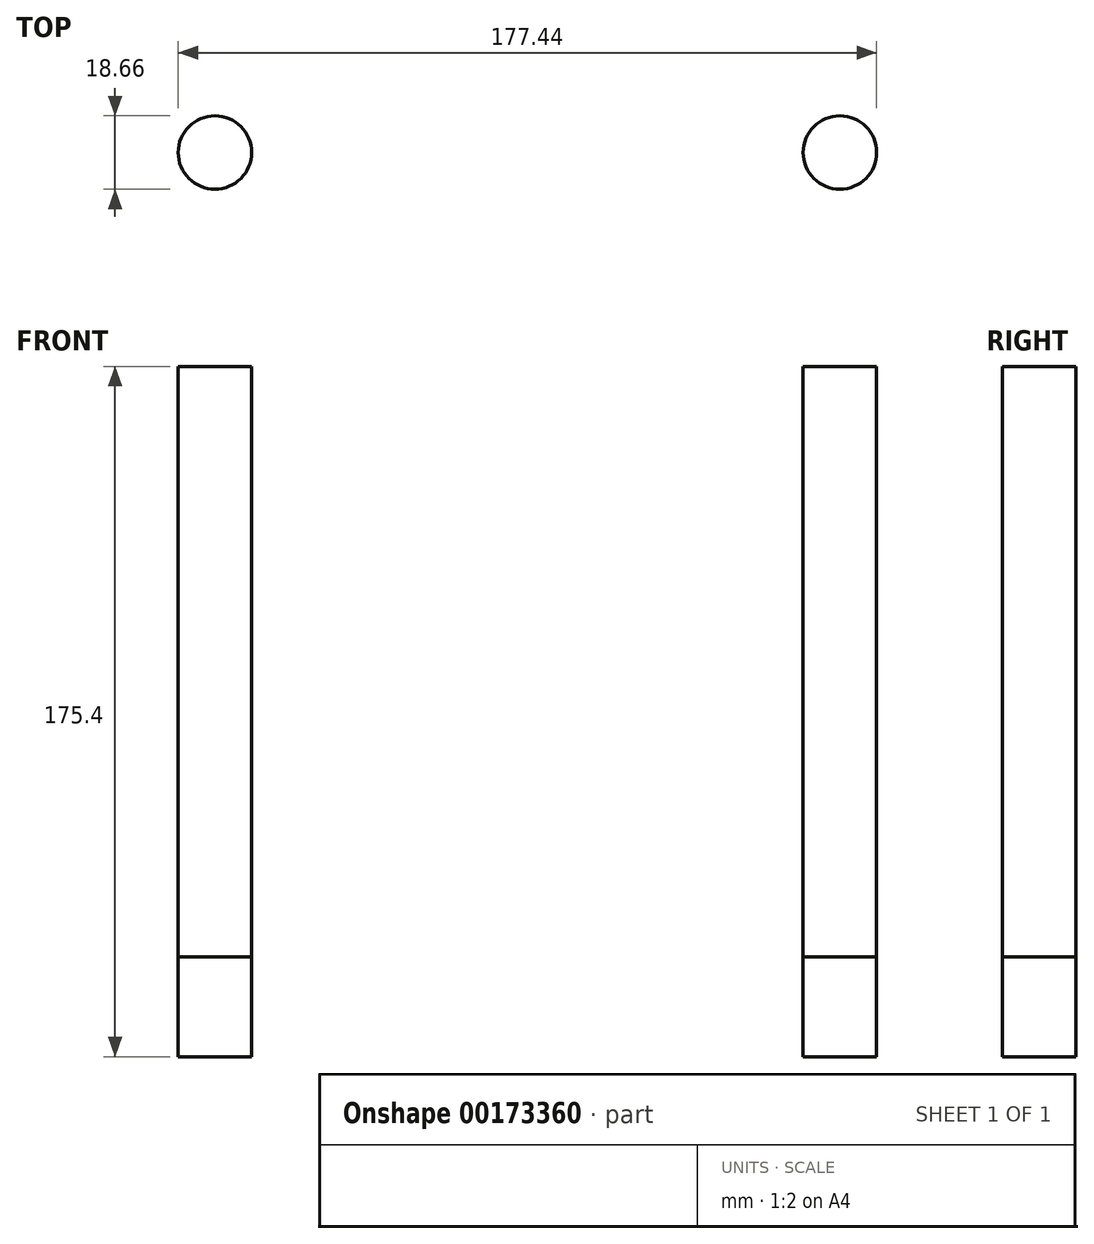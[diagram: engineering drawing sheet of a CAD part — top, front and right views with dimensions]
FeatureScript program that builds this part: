
annotation { "Feature Type Name" : "Feature", "Feature Type Description" : "" }
export const myFeature = defineFeature(function(context is Context, id is Id, definition is map)
    precondition{}
    {
        {
            var Q0;
            Q0=qCreatedBy(makeId("Top.planeOp"),FACE);
            var sketch = newSketch(context, id + "F0", { "sketchPlane" : qUnion([Q0])});
            skArc(sketch, "E0", {"start": v(88.89, 0) * mm, "mid": v(0, 88.89) * mm, "end": v(-88.89, 0) * mm});
            skArc(sketch, "E1", {"start": v(69.9, 0) * mm, "mid": v(0, 69.9) * mm, "end": v(-69.9, 0) * mm});
            skPoint(sketch, "E2.third.point", {"position": v(-77.17, 9.06) * mm});
            skPoint(sketch, "E3.third.point", {"position": v(77.17, 9.06) * mm});
            skLineSegment(sketch, "E4", {"start": v(-88.89, 0) * mm, "end": v(-69.9, 0) * mm, "construction": true});
            skLineSegment(sketch, "E5", {"start": v(69.9, 0) * mm, "end": v(88.89, 0) * mm, "construction": true});
            skCircle(sketch, "E6", {"center": v(-79.39, 0) * mm, "radius": 9.33 * mm});
            skCircle(sketch, "E7", {"center": v(79.39, 0) * mm, "radius": 9.33 * mm});
            skSolve(sketch);
        }
        {
            var Q0;
            Q0=sQuery(id+"F0.wireOp",EDGE,"E1");
            var Q1;
            Q1=sQuery(id+"F0.wireOp",EDGE,"E0");
            extrude(context, id + "F1", {"bodyType" : ToolBodyType.SURFACE, "surfaceEntities" : qUnion([Q0, Q1]), "depth" : 150 * mm});
        }
        {
            var Q0;
            Q0 = qSketchRegion(id + "F0", true);
            extrude(context, id + "F2", {"entities" : qUnion([Q0]), "depth" : 25.4 * mm});
        }
        {
            var Q0;
            Q0=makeQuery(id+"F2.opExtrude","CAP_FACE",FACE,{"disambiguationData":[OSD([sQuery(id+"F0.wireOp",EDGE,"E6")])],"isStart":false});
            var Q1;
            Q1=makeQuery(id+"F2.opExtrude","CAP_FACE",FACE,{"disambiguationData":[OSD([sQuery(id+"F0.wireOp",EDGE,"E7")])],"isStart":false});
            extrude(context, id + "F3", {"entities" : qUnion([Q0, Q1]), "depth" : 150 * mm});
        }
    });
